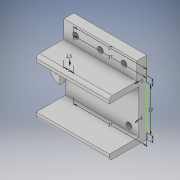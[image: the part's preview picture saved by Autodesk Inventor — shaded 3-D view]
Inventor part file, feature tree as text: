
AUTODESK INVENTOR PART (.ipt)
format: ipt  version: 2019 (Build 230136000, 136)  size: 312,832 bytes
history: native  units: mm
features: extrude x6, sketch x4, fillet x2, other x1, projected_geometry x1
ambient origin geometry x8: Origin, YZ Plane, XZ Plane, XY Plane, X Axis, Y Axis, Z Axis, Center Point
bodies: Body1 (feature_tree)
feature tree (14):
  other  "Bryła1"
  sketch  "Szkic1"
  extrude  "Wyciągnięcie proste1"  Depth=37.0mm
  extrude  "Wyciągnięcie proste2"  Depth=22.0mm
  extrude  "Wyciągnięcie proste3"  Depth=5.0mm
  extrude  "Wyciągnięcie proste4"  Depth=2.5mm
  fillet  "Zaokrąglenie2"  Radius=3.0mm
  fillet  "Zaokrąglenie3"  Radius=3.0mm
  extrude  "Wyciągnięcie proste5"  Depth=37.0mm
  extrude  "Wyciągnięcie proste6"  Depth=3.0mm
  sketch  "Szkic2"
  sketch  "Szkic3"
  projected_geometry  "Pętla rzutowana1"
  sketch  "Szkic4"
